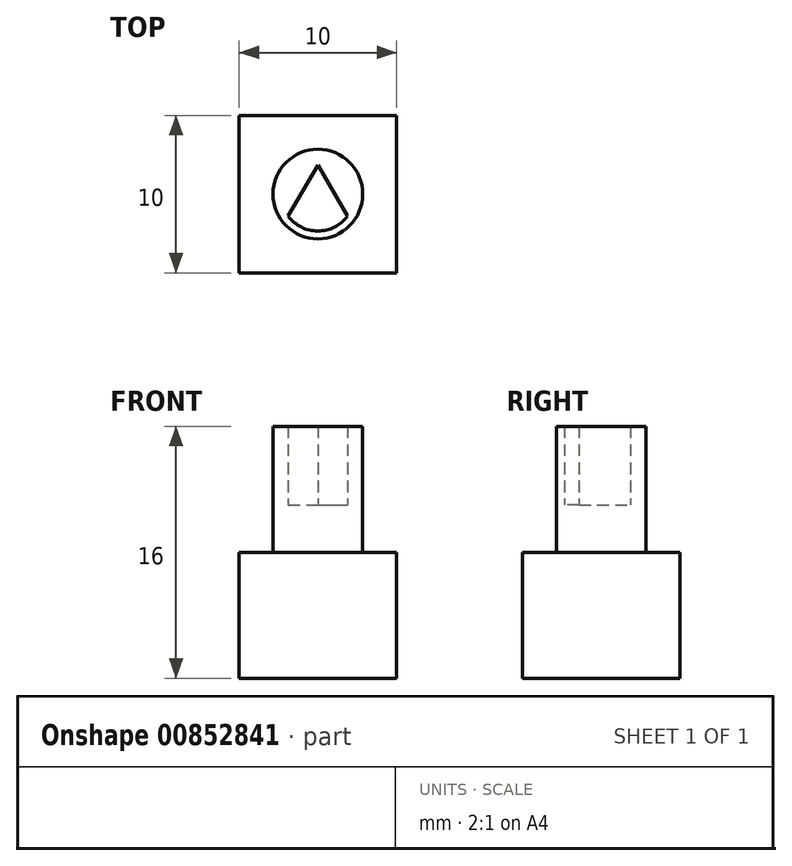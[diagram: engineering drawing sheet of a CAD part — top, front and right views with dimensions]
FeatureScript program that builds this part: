
annotation { "Feature Type Name" : "Feature", "Feature Type Description" : "" }
export const myFeature = defineFeature(function(context is Context, id is Id, definition is map)
    precondition{}
    {
        {
            var Q0;
            Q0=qCreatedBy(makeId("Top.planeOp"),FACE);
            var sketch = newSketch(context, id + "F0", { "sketchPlane" : qUnion([Q0])});
            skCircle(sketch, "E0", {"center": v(0, 0) * mm, "radius": 2.85 * mm});
            skCircle(sketch, "E1", {"center": v(0, 0) * mm, "radius": 2.35 * mm});
            skLineSegment(sketch, "E2", {"start": v(0, 2.85) * mm, "end": v(0, 1.85) * mm});
            skPoint(sketch, "E3.first.point", {"position": v(0, -2.35) * mm});
            skPoint(sketch, "E3.third.point", {"position": v(-1.71, 0) * mm});
            skLineSegment(sketch, "E4.0", {"start": v(0, 1.85) * mm, "end": v(1.56, -0.85) * mm});
            skLineSegment(sketch, "E4.2", {"start": v(-1.56, -0.85) * mm, "end": v(0, 1.85) * mm});
            skLineSegment(sketch, "E5", {"start": v(0, 1.85) * mm, "end": v(-1.88, -1.4) * mm});
            skLineSegment(sketch, "E6", {"start": v(0, 1.85) * mm, "end": v(1.88, -1.4) * mm});
            skSolve(sketch);
        }
        {
            var Q0;
            {var subQ0=sQuery(id+"F0.wireOp",EDGE,"E5");var subQ5=makeQuery(id+"F0.imprint","IMPRINT",VERTEX,{"derivedFrom":subQ0});Q0=makeQuery(id+"F0.imprint","IMPRINT",FACE,{"disambiguationData":[TD([[makeQuery(id+"F0.imprint","IMPRINT",EDGE,{"disambiguationData":[TD([[subQ5,-1.0]])],"derivedFrom":subQ0}),-1.0]])]});}
            var Q1;
            {var subQ0=sQuery(id+"F0.wireOp",EDGE,"E6");var subQ5=makeQuery(id+"F0.imprint","IMPRINT",VERTEX,{"derivedFrom":subQ0});Q1=makeQuery(id+"F0.imprint","IMPRINT",FACE,{"disambiguationData":[TD([[makeQuery(id+"F0.imprint","IMPRINT",EDGE,{"disambiguationData":[TD([[subQ5,-1.0]])],"derivedFrom":subQ0}),1.0]])]});}
            var Q2;
            Q2=makeQuery(id+"F0.imprint","IMPRINT",FACE,{"disambiguationData":[TD([[makeQuery(id+"F0.imprint","IMPRINT",EDGE,{"derivedFrom":sQuery(id+"F0.wireOp",EDGE,"E0")}),1.0]])]});
            extrude(context, id + "F1", {"entities" : qUnion([Q0, Q1, Q2]), "depth" : 8 * mm, "offsetDistance" : 25 * mm});
        }
        {
            var Q0;
            {var subQ0=sQuery(id+"F0.wireOp",EDGE,"E5");var subQ3=makeQuery(id+"F0.imprint","IMPRINT",VERTEX,{"derivedFrom":subQ0});Q0=makeQuery(id+"F0.imprint","IMPRINT",FACE,{"disambiguationData":[TD([[makeQuery(id+"F0.imprint","IMPRINT",EDGE,{"disambiguationData":[TD([[subQ3,-1.0]])],"derivedFrom":subQ0}),1.0]])]});}
            extrude(context, id + "F2", {"entities" : qUnion([Q0]), "operationType" : NewBodyOperationType.ADD, "depth" : 3 * mm, "offsetDistance" : 25 * mm});
        }
        {
            var Q0;
            Q0=qCreatedBy(makeId("Top.planeOp"),FACE);
            var sketch = newSketch(context, id + "F3", { "sketchPlane" : qUnion([Q0])});
            skLineSegment(sketch, "E7.bottom", {"start": v(-5, 5) * mm, "end": v(5, 5) * mm});
            skLineSegment(sketch, "E7.top", {"start": v(-5, -5) * mm, "end": v(5, -5) * mm});
            skLineSegment(sketch, "E7.left", {"start": v(-5, 5) * mm, "end": v(-5, -5) * mm});
            skLineSegment(sketch, "E7.right", {"start": v(5, 5) * mm, "end": v(5, -5) * mm});
            skSolve(sketch);
        }
        {
            var Q0;
            Q0=makeQuery(id+"F3.imprint","IMPRINT",FACE,{"disambiguationData":[TD([[makeQuery(id+"F3.imprint","IMPRINT",EDGE,{"derivedFrom":sQuery(id+"F3.wireOp",EDGE,"E7.bottom")}),-1.0]])]});
            extrude(context, id + "F4", {"entities" : qUnion([Q0]), "operationType" : NewBodyOperationType.ADD, "depth" : -8 * mm, "offsetDistance" : 25 * mm});
        }
    });
